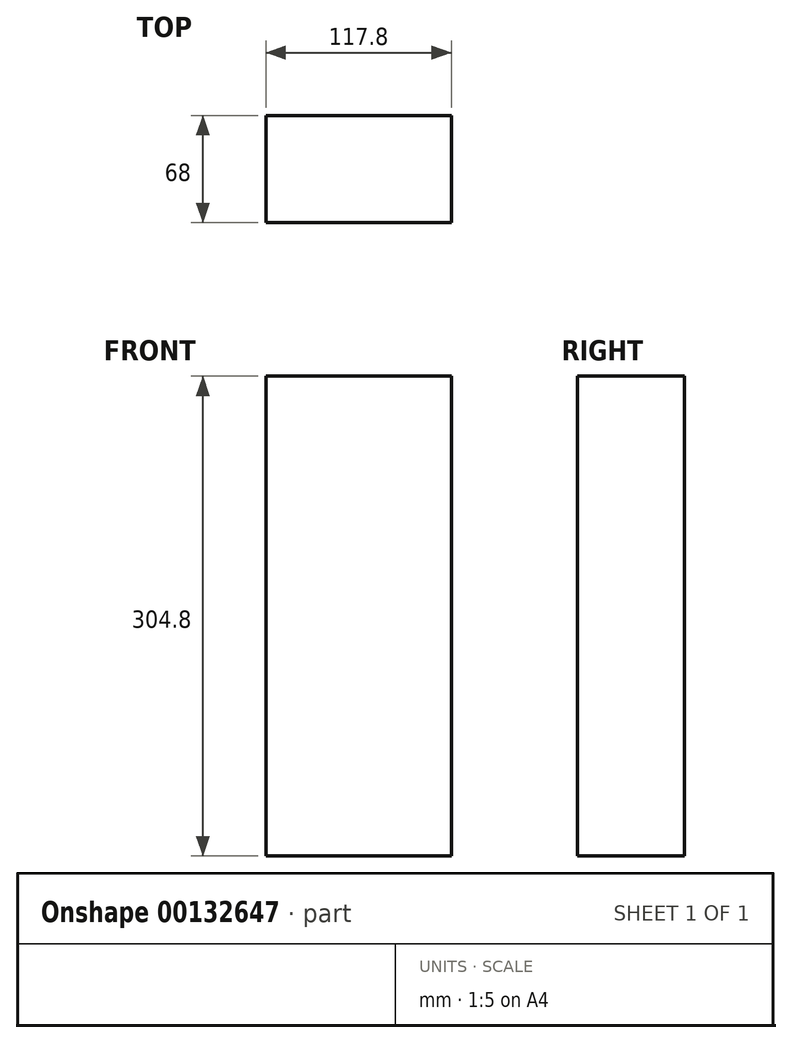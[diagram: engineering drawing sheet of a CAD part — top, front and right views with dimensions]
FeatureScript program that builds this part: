
annotation { "Feature Type Name" : "Feature", "Feature Type Description" : "" }
export const myFeature = defineFeature(function(context is Context, id is Id, definition is map)
    precondition{}
    {
        {
            var Q0;
            Q0=qCreatedBy(makeId("Top.planeOp"),FACE);
            var sketch = newSketch(context, id + "F0", { "sketchPlane" : qUnion([Q0])});
            skLineSegment(sketch, "E0.bottom", {"start": v(57, 68) * mm, "end": v(-60.8, 68) * mm});
            skLineSegment(sketch, "E0.top", {"start": v(57, 0) * mm, "end": v(-60.8, 0) * mm});
            skLineSegment(sketch, "E0.left", {"start": v(57, 68) * mm, "end": v(57, 0) * mm});
            skLineSegment(sketch, "E0.right", {"start": v(-60.8, 68) * mm, "end": v(-60.8, 0) * mm});
            skSolve(sketch);
        }
        {
            var Q0;
            Q0=makeQuery(id+"F0.imprint","IMPRINT",FACE,{"disambiguationData":[TD([[makeQuery(id+"F0.imprint","IMPRINT",EDGE,{"derivedFrom":sQuery(id+"F0.wireOp",EDGE,"E0.bottom")}),1.0]])]});
            extrude(context, id + "F1", {"entities" : qUnion([Q0]), "depth" : 304.8 * mm});
        }
    });
